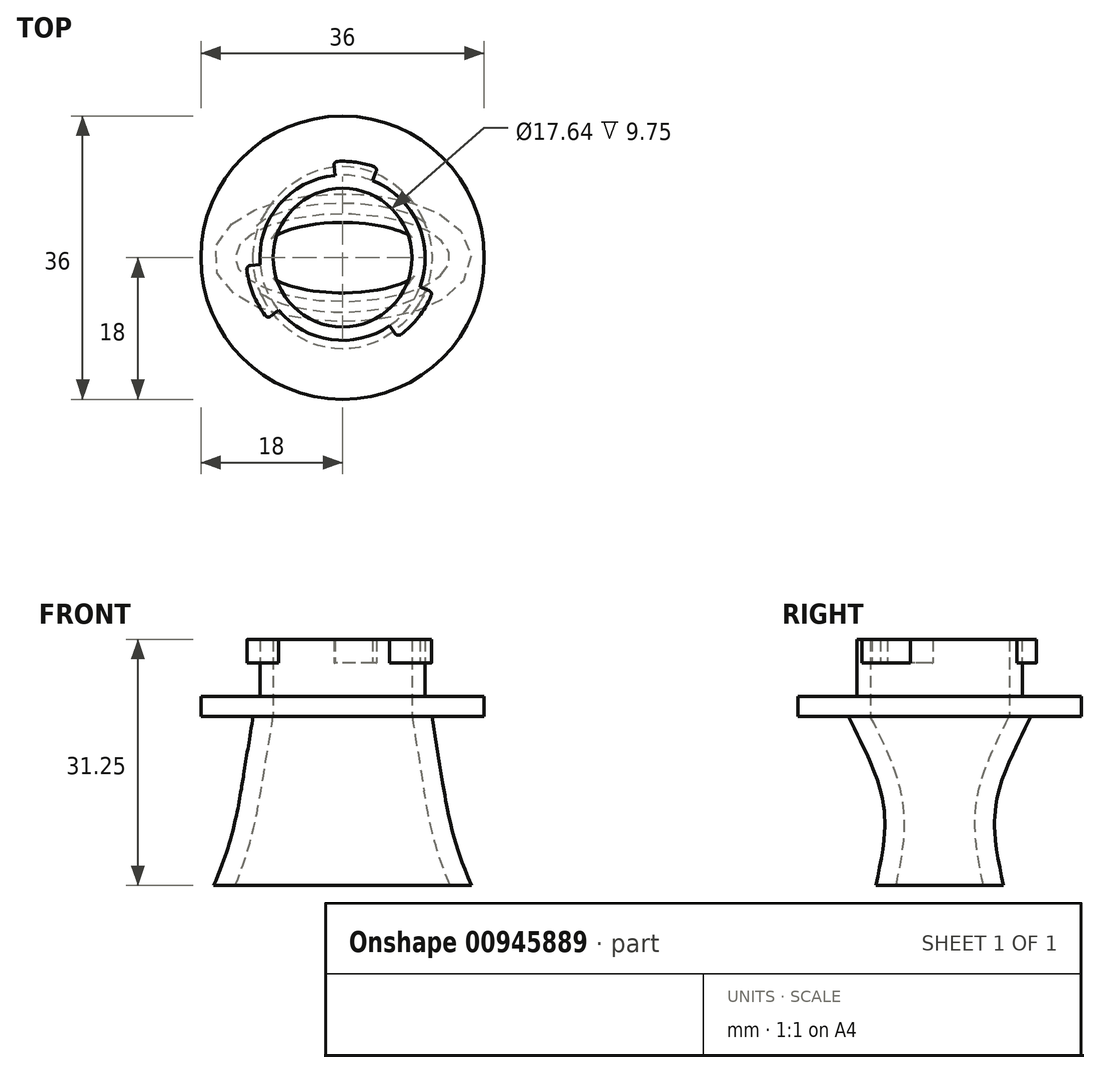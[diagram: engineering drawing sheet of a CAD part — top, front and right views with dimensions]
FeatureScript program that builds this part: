
annotation { "Feature Type Name" : "Feature", "Feature Type Description" : "" }
export const myFeature = defineFeature(function(context is Context, id is Id, definition is map)
    precondition{}
    {
        {
            assignVariable(context, id + "F0", {"name" : "distanceLayer", "anyValue" : 12 * mm});
        }
        {
            var Q0;
            Q0=qCreatedBy(makeId("Top.planeOp"),FACE);
            var sketch = newSketch(context, id + "F1", { "sketchPlane" : qUnion([Q0])});
            skCircle(sketch, "E0", {"center": v(0, 0) * mm, "radius": 8.82 * mm});
            skCircle(sketch, "E1", {"center": v(0, 0) * mm, "radius": 10.5 * mm});
            skCircle(sketch, "E2", {"center": v(0, 0) * mm, "radius": 12.25 * mm});
            skLineSegment(sketch, "E3", {"start": v(0, 0) * mm, "end": v(1.66, 11.8) * mm, "construction": true});
            skLineSegment(sketch, "E4", {"start": v(0, 0) * mm, "end": v(-10.85, -4.38) * mm, "construction": true});
            skLineSegment(sketch, "E5", {"start": v(0, 0) * mm, "end": v(9.22, -7.2) * mm, "construction": true});
            skLineSegment(sketch, "E6", {"start": v(0, 0) * mm, "end": v(-1.14, 12.2) * mm, "construction": true});
            skLineSegment(sketch, "E7", {"start": v(4.46, 11.4) * mm, "end": v(0, 0) * mm, "construction": true});
            skLineSegment(sketch, "E8", {"start": v(-12.2, -1.02) * mm, "end": v(0, 0) * mm, "construction": true});
            skLineSegment(sketch, "E9", {"start": v(-9.5, -7.74) * mm, "end": v(0, 0) * mm, "construction": true});
            skLineSegment(sketch, "E10", {"start": v(6.99, -10.06) * mm, "end": v(0, 0) * mm, "construction": true});
            skLineSegment(sketch, "E11", {"start": v(11.45, -4.35) * mm, "end": v(0, 0) * mm, "construction": true});
            skLineSegment(sketch, "E12", {"start": v(-1.14, 12.2) * mm, "end": v(4.46, 11.4) * mm, "construction": true});
            skLineSegment(sketch, "E13", {"start": v(6.99, -10.06) * mm, "end": v(11.45, -4.35) * mm, "construction": true});
            skLineSegment(sketch, "E14", {"start": v(-12.2, -1.02) * mm, "end": v(-9.5, -7.74) * mm, "construction": true});
            skLineSegment(sketch, "E15", {"start": v(-1.14, 12.2) * mm, "end": v(-0.98, 10.45) * mm});
            skLineSegment(sketch, "E16", {"start": v(4.46, 11.4) * mm, "end": v(3.82, 9.78) * mm});
            skLineSegment(sketch, "E17", {"start": v(-12.2, -1.02) * mm, "end": v(-10.46, -0.88) * mm});
            skLineSegment(sketch, "E18", {"start": v(-9.5, -7.74) * mm, "end": v(-8.14, -6.64) * mm});
            skLineSegment(sketch, "E19", {"start": v(6.99, -10.06) * mm, "end": v(6, -8.62) * mm});
            skLineSegment(sketch, "E20", {"start": v(11.45, -4.35) * mm, "end": v(9.82, -3.73) * mm});
            skCircle(sketch, "E21", {"center": v(0, 0) * mm, "radius": 18 * mm});
            skLineSegment(sketch, "E22", {"start": v(0, 0) * mm, "end": v(0, 25.46) * mm, "construction": true});
            skSolve(sketch);
        }
        {
            var Q0;
            Q0=makeQuery(id+"F1.imprint","IMPRINT",FACE,{"disambiguationData":[TD([[makeQuery(id+"F1.imprint","IMPRINT",EDGE,{"derivedFrom":sQuery(id+"F1.wireOp",EDGE,"E0")}),-1.0]])]});
            extrude(context, id + "F2", {"entities" : qUnion([Q0]), "depth" : 7.25 * mm, "offsetDistance" : 25 * mm});
        }
        {
            var Q0;
            {var subQ0=sQuery(id+"F1.wireOp",EDGE,"E17");Q0=makeQuery(id+"F1.imprint","IMPRINT",FACE,{"disambiguationData":[TD([[makeQuery(id+"F1.imprint","IMPRINT",EDGE,{"derivedFrom":subQ0}),-1.0]])]});}
            var Q1;
            {var subQ0=sQuery(id+"F1.wireOp",EDGE,"E19");Q1=makeQuery(id+"F1.imprint","IMPRINT",FACE,{"disambiguationData":[TD([[makeQuery(id+"F1.imprint","IMPRINT",EDGE,{"derivedFrom":subQ0}),-1.0]])]});}
            var Q2;
            {var subQ0=sQuery(id+"F1.wireOp",EDGE,"E15");Q2=makeQuery(id+"F1.imprint","IMPRINT",FACE,{"disambiguationData":[TD([[makeQuery(id+"F1.imprint","IMPRINT",EDGE,{"derivedFrom":subQ0}),1.0]])]});}
            extrude(context, id + "F3", {"entities" : qUnion([Q0, Q1, Q2]), "operationType" : NewBodyOperationType.ADD, "depth" : 7.25 * mm, "offsetDistance" : 25 * mm, "hasSecondDirection" : true, "secondDirectionOppositeDirection" : false, "secondDirectionDepth" : 4.25 * mm});
        }
        {
            var Q0;
            Q0=makeQuery(id+"F1.imprint","IMPRINT",FACE,{"disambiguationData":[TD([[makeQuery(id+"F1.imprint","IMPRINT",EDGE,{"derivedFrom":sQuery(id+"F1.wireOp",EDGE,"E0")}),-1.0]])]});
            var Q1;
            {var subQ0=sQuery(id+"F1.wireOp",EDGE,"E18");Q1=makeQuery(id+"F1.imprint","IMPRINT",FACE,{"disambiguationData":[TD([[makeQuery(id+"F1.imprint","IMPRINT",EDGE,{"derivedFrom":subQ0}),-1.0]])]});}
            var Q2;
            {var subQ0=sQuery(id+"F1.wireOp",EDGE,"E19");Q2=makeQuery(id+"F1.imprint","IMPRINT",FACE,{"disambiguationData":[TD([[makeQuery(id+"F1.imprint","IMPRINT",EDGE,{"derivedFrom":subQ0}),-1.0]])]});}
            var Q3;
            {var subQ0=sQuery(id+"F1.wireOp",EDGE,"E16");Q3=makeQuery(id+"F1.imprint","IMPRINT",FACE,{"disambiguationData":[TD([[makeQuery(id+"F1.imprint","IMPRINT",EDGE,{"derivedFrom":subQ0}),1.0]])]});}
            var Q4;
            {var subQ0=sQuery(id+"F1.wireOp",EDGE,"E15");Q4=makeQuery(id+"F1.imprint","IMPRINT",FACE,{"disambiguationData":[TD([[makeQuery(id+"F1.imprint","IMPRINT",EDGE,{"derivedFrom":subQ0}),1.0]])]});}
            var Q5;
            {var subQ0=sQuery(id+"F1.wireOp",EDGE,"E15");Q5=makeQuery(id+"F1.imprint","IMPRINT",FACE,{"disambiguationData":[TD([[makeQuery(id+"F1.imprint","IMPRINT",EDGE,{"derivedFrom":subQ0}),-1.0]])]});}
            var Q6;
            Q6=makeQuery(id+"F1.imprint","IMPRINT",FACE,{"disambiguationData":[TD([[makeQuery(id+"F1.imprint","IMPRINT",EDGE,{"derivedFrom":sQuery(id+"F1.wireOp",EDGE,"E21")}),1.0]])]});
            var Q7;
            {var subQ0=sQuery(id+"F1.wireOp",EDGE,"E17");Q7=makeQuery(id+"F1.imprint","IMPRINT",FACE,{"disambiguationData":[TD([[makeQuery(id+"F1.imprint","IMPRINT",EDGE,{"derivedFrom":subQ0}),-1.0]])]});}
            extrude(context, id + "F4", {"entities" : qUnion([Q0, Q1, Q2, Q3, Q4, Q5, Q6, Q7]), "operationType" : NewBodyOperationType.ADD, "oppositeDirection" : true, "depth" : 2.5 * mm, "offsetDistance" : 25 * mm});
        }
        {
            var Q0;
            Q0=makeQuery(id+"F2.opExtrude","CAP_EDGE",EDGE,{"disambiguationData":[OSD([sQuery(id+"F1.wireOp",EDGE,"E1")])],"isStart":true});
            var Q1;
            Q1=makeQuery(id+"F3.opExtrude","SWEPT_EDGE",EDGE,{"disambiguationData":[OSD([sQuery(id+"F1.wireOp",EDGE,"E1"),sQuery(id+"F1.wireOp",EDGE,"E18")])]});
            var Q2;
            Q2=makeQuery(id+"F3.opExtrude","SWEPT_EDGE",EDGE,{"disambiguationData":[OSD([sQuery(id+"F1.wireOp",EDGE,"E1"),sQuery(id+"F1.wireOp",EDGE,"E19")])]});
            var Q3;
            Q3=makeQuery(id+"F3.opExtrude","SWEPT_EDGE",EDGE,{"disambiguationData":[OSD([sQuery(id+"F1.wireOp",EDGE,"E2"),sQuery(id+"F1.wireOp",EDGE,"E19")])]});
            var Q4;
            Q4=makeQuery(id+"F3.opExtrude","SWEPT_EDGE",EDGE,{"disambiguationData":[OSD([sQuery(id+"F1.wireOp",EDGE,"E2"),sQuery(id+"F1.wireOp",EDGE,"E18")])]});
            var Q5;
            Q5=makeQuery(id+"F3.opExtrude","SWEPT_EDGE",EDGE,{"disambiguationData":[OSD([sQuery(id+"F1.wireOp",EDGE,"E2"),sQuery(id+"F1.wireOp",EDGE,"E17")])]});
            var Q6;
            Q6=makeQuery(id+"F3.opExtrude","SWEPT_EDGE",EDGE,{"disambiguationData":[OSD([sQuery(id+"F1.wireOp",EDGE,"E1"),sQuery(id+"F1.wireOp",EDGE,"E17")])]});
            var Q7;
            Q7=makeQuery(id+"F3.opExtrude","SWEPT_EDGE",EDGE,{"disambiguationData":[OSD([sQuery(id+"F1.wireOp",EDGE,"E1"),sQuery(id+"F1.wireOp",EDGE,"E15")])]});
            var Q8;
            Q8=makeQuery(id+"F3.opExtrude","SWEPT_EDGE",EDGE,{"disambiguationData":[OSD([sQuery(id+"F1.wireOp",EDGE,"E2"),sQuery(id+"F1.wireOp",EDGE,"E15")])]});
            var Q9;
            Q9=makeQuery(id+"F3.opExtrude","SWEPT_EDGE",EDGE,{"disambiguationData":[OSD([sQuery(id+"F1.wireOp",EDGE,"E2"),sQuery(id+"F1.wireOp",EDGE,"E16")])]});
            var Q10;
            Q10=makeQuery(id+"F3.opExtrude","SWEPT_EDGE",EDGE,{"disambiguationData":[OSD([sQuery(id+"F1.wireOp",EDGE,"E1"),sQuery(id+"F1.wireOp",EDGE,"E16")])]});
            var Q11;
            Q11=makeQuery(id+"F3.opExtrude","SWEPT_EDGE",EDGE,{"disambiguationData":[OSD([sQuery(id+"F1.wireOp",EDGE,"E1"),sQuery(id+"F1.wireOp",EDGE,"E20")])]});
            var Q12;
            Q12=makeQuery(id+"F3.opExtrude","SWEPT_EDGE",EDGE,{"disambiguationData":[OSD([sQuery(id+"F1.wireOp",EDGE,"E2"),sQuery(id+"F1.wireOp",EDGE,"E20")])]});
            fillet(context, id + "F5", {"entities" : qUnion([Q0, Q1, Q2, Q3, Q4, Q5, Q6, Q7, Q8, Q9, Q10, Q11, Q12]), "radius" : 0.5 * mm, "tangentPropagation" : true, "allowEdgeOverflow" : false});
        }
        {
            var Q0;
            Q0=qCreatedBy(makeId("Top.planeOp"),FACE);
            cPlane(context, id + "F6", {"entities" : qUnion([Q0]), "cplaneType" : CPlaneType.OFFSET, "offset" : 2.5 * mm, "oppositeDirection" : true, "width" : 150 * mm, "height" : 150 * mm});
        }
        {
            var Q0;
            Q0=qCreatedBy(makeId("Top.planeOp"),FACE);
            cPlane(context, id + "F7", {"entities" : qUnion([Q0]), "cplaneType" : CPlaneType.OFFSET, "offset" : getVariable(context, 'distanceLayer'), "oppositeDirection" : true, "width" : 150 * mm, "height" : 150 * mm});
        }
        {
            var Q0;
            Q0=qCreatedBy(id+"F7.planeOp",FACE);
            cPlane(context, id + "F8", {"entities" : qUnion([Q0]), "cplaneType" : CPlaneType.OFFSET, "offset" : getVariable(context, 'distanceLayer'), "oppositeDirection" : true, "width" : 150 * mm, "height" : 150 * mm});
        }
        {
            var Q0;
            Q0=qCreatedBy(id+"F6.planeOp",FACE);
            var sketch = newSketch(context, id + "F9", { "sketchPlane" : qUnion([Q0])});
            skCircle(sketch, "E23", {"center": v(0, 0) * mm, "radius": 8.82 * mm});
            skCircle(sketch, "E24", {"center": v(0, 0) * mm, "radius": 17 * mm});
            skSolve(sketch);
        }
        {
            var Q0;
            Q0=qCreatedBy(id+"F7.planeOp",FACE);
            var sketch = newSketch(context, id + "F10", { "sketchPlane" : qUnion([Q0])});
            skEllipse(sketch, "E25", {"center": v(0, 0) * mm, "majorRadius": 18 * mm, "minorRadius": 8 * mm, "majorAxis": v(1, 0)});
            skEllipse(sketch, "E26", {"center": v(0, 0) * mm, "majorRadius": 10.37 * mm, "minorRadius": 4.94 * mm, "majorAxis": v(1, 0)});
            skSolve(sketch);
        }
        {
            var Q0;
            Q0=qCreatedBy(id+"F8.planeOp",FACE);
            var sketch = newSketch(context, id + "F11", { "sketchPlane" : qUnion([Q0])});
            skEllipse(sketch, "E27", {"center": v(0, 0) * mm, "majorRadius": 18 * mm, "minorRadius": 8 * mm, "majorAxis": v(-1, 0)});
            skEllipse(sketch, "E28", {"center": v(0, 0) * mm, "majorRadius": 13.65 * mm, "minorRadius": 5.56 * mm, "majorAxis": v(1, 0)});
            skSolve(sketch);
        }
        {
            var Q1;
            Q1=makeQuery(id+"F9.imprint","IMPRINT",FACE,{"disambiguationData":[TD([[makeQuery(id+"F9.imprint","IMPRINT",EDGE,{"derivedFrom":sQuery(id+"F9.wireOp",EDGE,"E23")}),1.0]])]});
            var Q2;
            Q2=makeQuery(id+"F10.imprint","IMPRINT",FACE,{"disambiguationData":[TD([[makeQuery(id+"F10.imprint","IMPRINT",EDGE,{"derivedFrom":sQuery(id+"F10.wireOp",EDGE,"E26")}),1.0]])]});
            var Q3;
            Q3=makeQuery(id+"F11.imprint","IMPRINT",FACE,{"disambiguationData":[TD([[makeQuery(id+"F11.imprint","IMPRINT",EDGE,{"derivedFrom":sQuery(id+"F11.wireOp",EDGE,"E28")}),1.0]])]});
            loft(context, id + "F12", {"sheetProfilesArray" : [{ "sheetProfileEntities" : qUnion([Q1]) }, { "sheetProfileEntities" : qUnion([Q2]) }, { "sheetProfileEntities" : qUnion([Q3]) }]});
        }
        {
            var Q0;
            Q0=makeQuery(id+"F12.opLoft","CAP_FACE",FACE,{"disambiguationData":[OSD([makeQuery(id+"F11.imprint","IMPRINT",FACE,{"disambiguationData":[TD([[makeQuery(id+"F11.imprint","IMPRINT",EDGE,{"derivedFrom":sQuery(id+"F11.wireOp",EDGE,"E28")}),1.0]])]})])],"isStart":true});
            var Q1;
            Q1=makeQuery(id+"F12.opLoft","CAP_FACE",FACE,{"disambiguationData":[OSD([makeQuery(id+"F9.imprint","IMPRINT",FACE,{"disambiguationData":[TD([[makeQuery(id+"F9.imprint","IMPRINT",EDGE,{"derivedFrom":sQuery(id+"F9.wireOp",EDGE,"E23")}),1.0]])]})])],"isStart":true});
            shell(context, id + "F13", {"entities" : qUnion([Q0, Q1]), "thickness" : 2.5 * mm, "oppositeDirection" : true});
        }
    });
